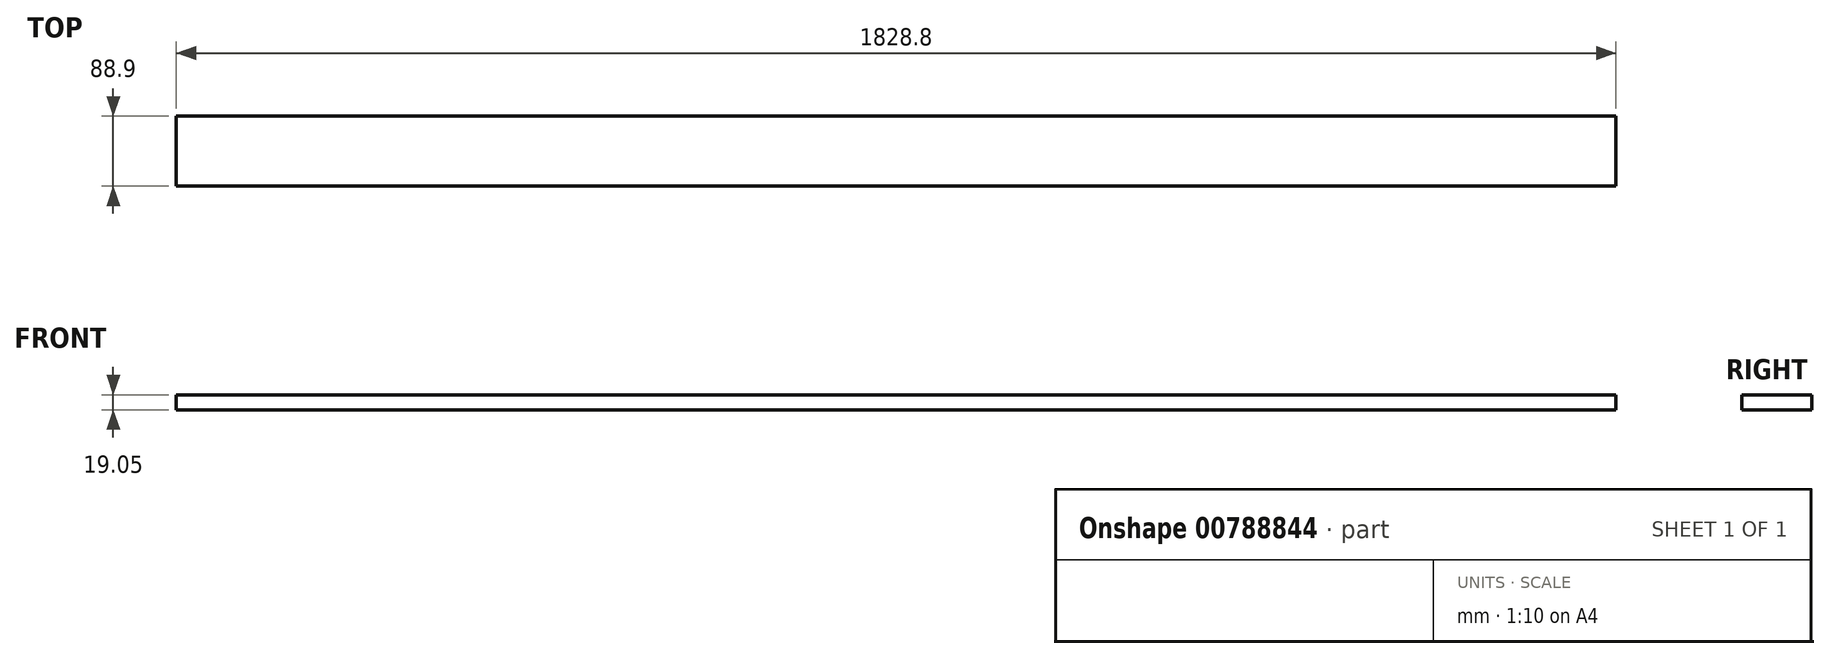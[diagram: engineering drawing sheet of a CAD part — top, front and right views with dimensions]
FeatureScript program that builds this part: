
annotation { "Feature Type Name" : "Feature", "Feature Type Description" : "" }
export const myFeature = defineFeature(function(context is Context, id is Id, definition is map)
    precondition{}
    {
        {
            var Q0;
            Q0=qCreatedBy(makeId("Top.planeOp"),FACE);
            var sketch = newSketch(context, id + "F0", { "sketchPlane" : qUnion([Q0])});
            skLineSegment(sketch, "E0.bottom", {"start": v(0, 0) * mm, "end": v(1828.8, 0) * mm});
            skLineSegment(sketch, "E0.top", {"start": v(0, 88.9) * mm, "end": v(1828.8, 88.9) * mm});
            skLineSegment(sketch, "E0.left", {"start": v(0, 0) * mm, "end": v(0, 88.9) * mm});
            skLineSegment(sketch, "E0.right", {"start": v(1828.8, 0) * mm, "end": v(1828.8, 88.9) * mm});
            skSolve(sketch);
        }
        {
            var Q0;
            Q0=makeQuery(id+"F0.imprint","IMPRINT",FACE,{"disambiguationData":[TD([[makeQuery(id+"F0.imprint","IMPRINT",EDGE,{"derivedFrom":sQuery(id+"F0.wireOp",EDGE,"E0.bottom")}),1.0]])]});
            extrude(context, id + "F1", {"entities" : qUnion([Q0]), "depth" : 19.05 * mm, "offsetDistance" : 25.4 * mm});
        }
    });
